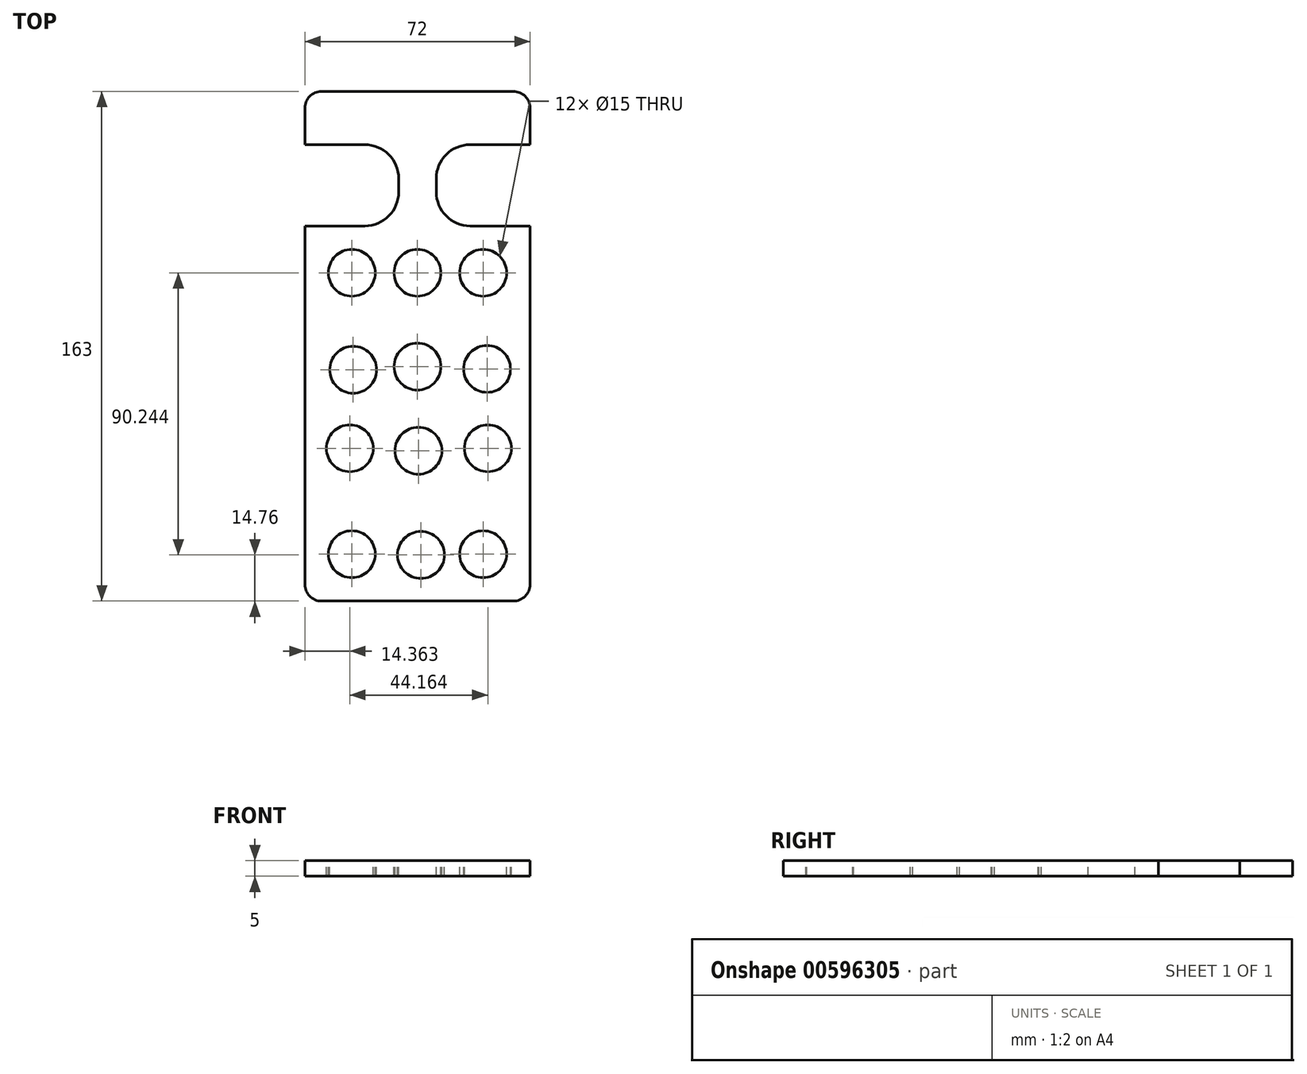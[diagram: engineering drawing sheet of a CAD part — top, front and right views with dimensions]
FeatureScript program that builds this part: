
annotation { "Feature Type Name" : "Feature", "Feature Type Description" : "" }
export const myFeature = defineFeature(function(context is Context, id is Id, definition is map)
    precondition{}
    {
        {
            var Q0;
            Q0=qCreatedBy(makeId("Top.planeOp"),FACE);
            var sketch = newSketch(context, id + "F0", { "sketchPlane" : qUnion([Q0])});
            skLineSegment(sketch, "E0.bottom", {"start": v(-44.34, 126.57) * mm, "end": v(27.66, 126.57) * mm});
            skLineSegment(sketch, "E0.top", {"start": v(-44.34, -36.43) * mm, "end": v(27.66, -36.43) * mm});
            skLineSegment(sketch, "E0.left", {"start": v(-44.34, 126.57) * mm, "end": v(-44.34, -36.43) * mm});
            skLineSegment(sketch, "E0.right", {"start": v(27.66, 126.57) * mm, "end": v(27.66, -36.43) * mm});
            skSolve(sketch);
        }
        {
            var Q0;
            Q0=qSketchRegion(id+"F0",true);
            extrude(context, id + "F1", {"entities" : qUnion([Q0]), "oppositeDirection" : true, "depth" : 5 * mm, "offsetDistance" : 25 * mm});
        }
        {
            var Q0;
            Q0=makeQuery(id+"F0.imprint","IMPRINT",FACE,{"disambiguationData":[TD([[makeQuery(id+"F0.imprint","IMPRINT",EDGE,{"derivedFrom":sQuery(id+"F0.wireOp",EDGE,"E0.bottom")}),-1.0]])]});
            var sketch = newSketch(context, id + "F2", { "sketchPlane" : qUnion([Q0])});
            skLineSegment(sketch, "E1.bottom", {"start": v(27.66, 109.57) * mm, "end": v(-2.34, 109.57) * mm});
            skLineSegment(sketch, "E1.top", {"start": v(27.66, 83.57) * mm, "end": v(-2.34, 83.57) * mm});
            skLineSegment(sketch, "E1.left", {"start": v(27.66, 109.57) * mm, "end": v(27.66, 83.57) * mm});
            skLineSegment(sketch, "E1.right", {"start": v(-2.34, 109.57) * mm, "end": v(-2.34, 83.57) * mm});
            skLineSegment(sketch, "E2.bottom", {"start": v(-44.34, 109.57) * mm, "end": v(-14.34, 109.57) * mm});
            skLineSegment(sketch, "E2.top", {"start": v(-44.34, 83.57) * mm, "end": v(-14.34, 83.57) * mm});
            skLineSegment(sketch, "E2.left", {"start": v(-44.34, 109.57) * mm, "end": v(-44.34, 83.57) * mm});
            skLineSegment(sketch, "E2.right", {"start": v(-14.34, 109.57) * mm, "end": v(-14.34, 83.57) * mm});
            skCircle(sketch, "E3", {"center": v(12.66, 68.57) * mm, "radius": 7.5 * mm});
            skCircle(sketch, "E4", {"center": v(-29.34, 68.57) * mm, "radius": 7.5 * mm});
            skCircle(sketch, "E5", {"center": v(-8.34, 38.57) * mm, "radius": 7.5 * mm});
            skCircle(sketch, "E6", {"center": v(-29.34, -21.43) * mm, "radius": 7.5 * mm});
            skCircle(sketch, "E7", {"center": v(12.66, -21.43) * mm, "radius": 7.5 * mm});
            skCircle(sketch, "E8", {"center": v(-8.34, 68.57) * mm, "radius": 7.5 * mm});
            skCircle(sketch, "E9", {"center": v(-28.92, 37.57) * mm, "radius": 7.5 * mm});
            skCircle(sketch, "E10", {"center": v(13.92, 37.83) * mm, "radius": 7.5 * mm});
            skCircle(sketch, "E11", {"center": v(-8.03, 11.65) * mm, "radius": 7.5 * mm});
            skCircle(sketch, "E12", {"center": v(-29.98, 12.44) * mm, "radius": 7.5 * mm});
            skCircle(sketch, "E13", {"center": v(14.19, 12.44) * mm, "radius": 7.5 * mm});
            skCircle(sketch, "E14", {"center": v(-7.23, -21.67) * mm, "radius": 7.5 * mm});
            skSolve(sketch);
        }
        {
            var Q0;
            Q0=qSketchRegion(id+"F2",true);
            extrude(context, id + "F3", {"entities" : qUnion([Q0]), "operationType" : NewBodyOperationType.REMOVE, "oppositeDirection" : true, "depth" : 25 * mm, "offsetDistance" : 25 * mm});
        }
        {
            var Q0;
            Q0=makeQuery(id+"F3.boolean.opBoolean","COPY",EDGE,{"derivedFrom":makeQuery(id+"F3.opExtrude","SWEPT_EDGE",EDGE,{"disambiguationData":[OSD([sQuery(id+"F2.wireOp",EDGE,"E1.bottom"),sQuery(id+"F2.wireOp",EDGE,"E1.right")])]})});
            var Q1;
            Q1=makeQuery(id+"F3.boolean.opBoolean","COPY",EDGE,{"derivedFrom":makeQuery(id+"F3.opExtrude","SWEPT_EDGE",EDGE,{"disambiguationData":[OSD([sQuery(id+"F2.wireOp",EDGE,"E1.top"),sQuery(id+"F2.wireOp",EDGE,"E1.right")])]})});
            var Q2;
            Q2=makeQuery(id+"F3.boolean.opBoolean","COPY",EDGE,{"derivedFrom":makeQuery(id+"F3.opExtrude","SWEPT_EDGE",EDGE,{"disambiguationData":[OSD([sQuery(id+"F2.wireOp",EDGE,"E2.top"),sQuery(id+"F2.wireOp",EDGE,"E2.right")])]})});
            var Q3;
            Q3=makeQuery(id+"F3.boolean.opBoolean","COPY",EDGE,{"derivedFrom":makeQuery(id+"F3.opExtrude","SWEPT_EDGE",EDGE,{"disambiguationData":[OSD([sQuery(id+"F2.wireOp",EDGE,"E2.bottom"),sQuery(id+"F2.wireOp",EDGE,"E2.right")])]})});
            fillet(context, id + "F4", {"entities" : qUnion([Q0, Q1, Q2, Q3]), "radius" : 10.86 * mm, "tangentPropagation" : true, "allowEdgeOverflow" : false});
        }
        {
            var Q0;
            Q0=makeQuery(id+"F1.opExtrude","SWEPT_EDGE",EDGE,{"disambiguationData":[OSD([sQuery(id+"F0.wireOp",EDGE,"E0.bottom"),sQuery(id+"F0.wireOp",EDGE,"E0.right")])]});
            var Q1;
            Q1=makeQuery(id+"F1.opExtrude","SWEPT_EDGE",EDGE,{"disambiguationData":[OSD([sQuery(id+"F0.wireOp",EDGE,"E0.bottom"),sQuery(id+"F0.wireOp",EDGE,"E0.left")])]});
            var Q2;
            Q2=makeQuery(id+"F3.boolean.opBoolean","COPY",EDGE,{"derivedFrom":makeQuery(id+"F3.opExtrude","SWEPT_EDGE",EDGE,{"disambiguationData":[OSD([sQuery(id+"F0.wireOp",EDGE,"E0.left"),sQuery(id+"F2.wireOp",EDGE,"E2.bottom"),sQuery(id+"F2.wireOp",EDGE,"E2.left")])]})});
            var Q3;
            Q3=makeQuery(id+"F3.boolean.opBoolean","COPY",EDGE,{"derivedFrom":makeQuery(id+"F3.opExtrude","SWEPT_EDGE",EDGE,{"disambiguationData":[OSD([sQuery(id+"F0.wireOp",EDGE,"E0.left"),sQuery(id+"F2.wireOp",EDGE,"E2.top"),sQuery(id+"F2.wireOp",EDGE,"E2.left")])]})});
            var Q4;
            Q4=makeQuery(id+"F3.boolean.opBoolean","COPY",EDGE,{"derivedFrom":makeQuery(id+"F3.opExtrude","SWEPT_EDGE",EDGE,{"disambiguationData":[OSD([sQuery(id+"F0.wireOp",EDGE,"E0.right"),sQuery(id+"F2.wireOp",EDGE,"E1.bottom"),sQuery(id+"F2.wireOp",EDGE,"E1.left")])]})});
            var Q5;
            Q5=makeQuery(id+"F3.boolean.opBoolean","COPY",EDGE,{"derivedFrom":makeQuery(id+"F3.opExtrude","SWEPT_EDGE",EDGE,{"disambiguationData":[OSD([sQuery(id+"F0.wireOp",EDGE,"E0.right"),sQuery(id+"F2.wireOp",EDGE,"E1.top"),sQuery(id+"F2.wireOp",EDGE,"E1.left")])]})});
            var Q6;
            Q6=makeQuery(id+"F1.opExtrude","SWEPT_EDGE",EDGE,{"disambiguationData":[OSD([sQuery(id+"F0.wireOp",EDGE,"E0.top"),sQuery(id+"F0.wireOp",EDGE,"E0.left")])]});
            var Q7;
            Q7=makeQuery(id+"F1.opExtrude","SWEPT_EDGE",EDGE,{"disambiguationData":[OSD([sQuery(id+"F0.wireOp",EDGE,"E0.top"),sQuery(id+"F0.wireOp",EDGE,"E0.right")])]});
            fillet(context, id + "F5", {"entities" : qUnion([Q0, Q1, Q2, Q3, Q4, Q5, Q6, Q7]), "radius" : 5.3 * mm, "tangentPropagation" : true, "allowEdgeOverflow" : false});
        }
    });
